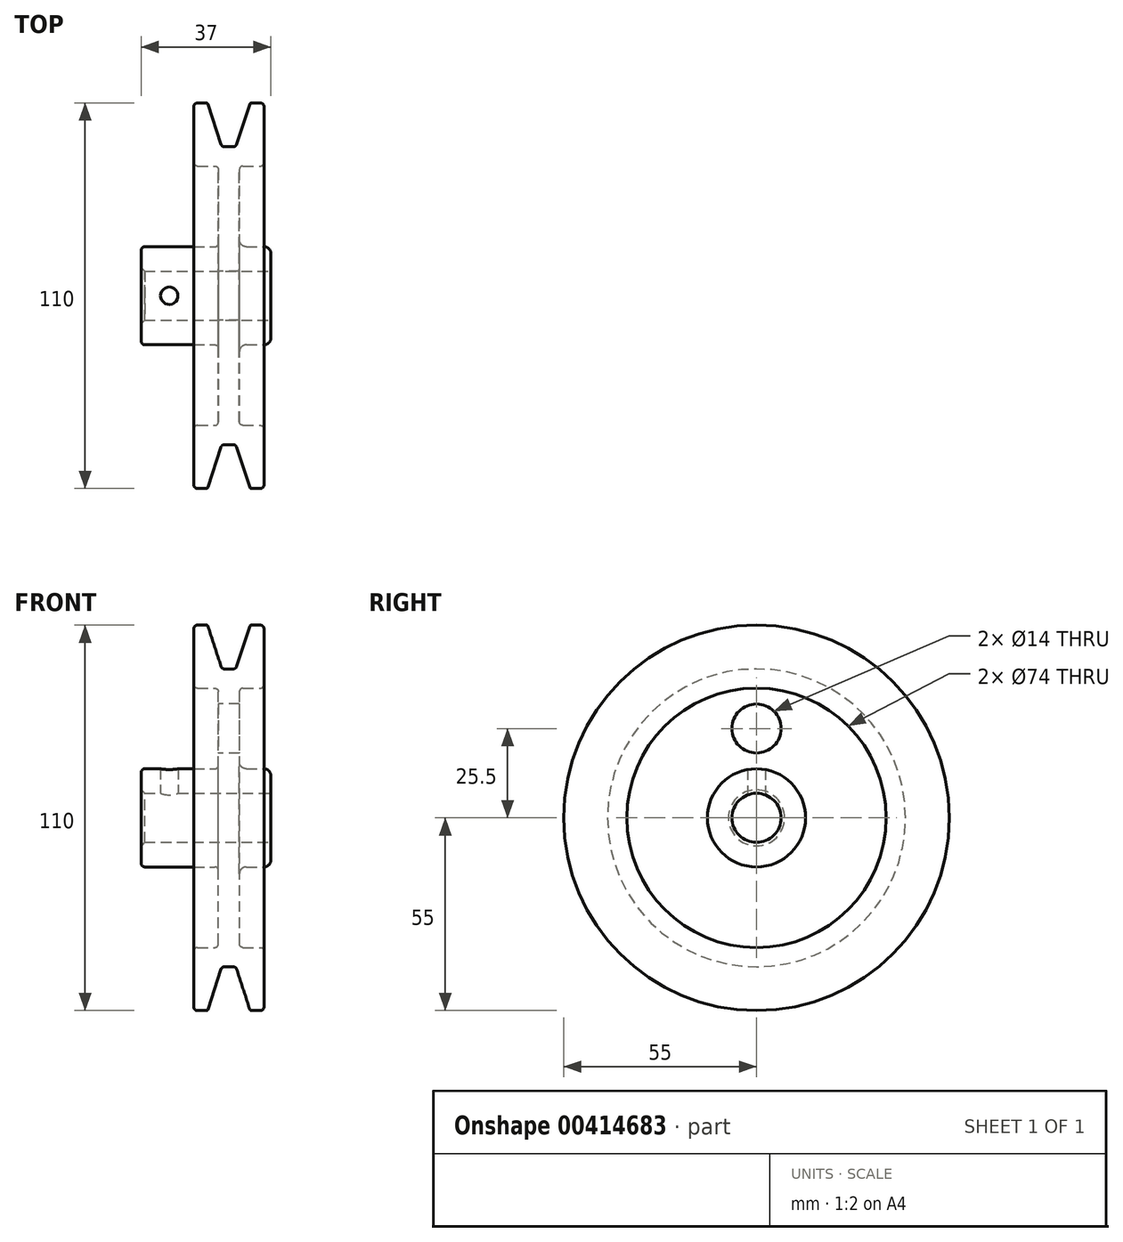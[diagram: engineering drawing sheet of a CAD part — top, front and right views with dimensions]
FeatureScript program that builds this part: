
annotation { "Feature Type Name" : "Feature", "Feature Type Description" : "" }
export const myFeature = defineFeature(function(context is Context, id is Id, definition is map)
    precondition{}
    {
        {
            var Q0;
            Q0=qCreatedBy(makeId("Front.planeOp"),FACE);
            var sketch = newSketch(context, id + "F0", { "sketchPlane" : qUnion([Q0])});
            skLineSegment(sketch, "E0", {"start": v(0, 0) * mm, "end": v(-34.66, 0) * mm, "construction": true});
            skLineSegment(sketch, "E1", {"start": v(0, 7) * mm, "end": v(-37, 7) * mm});
            skLineSegment(sketch, "E2", {"start": v(-37, 7) * mm, "end": v(-37, 14) * mm});
            skLineSegment(sketch, "E3", {"start": v(-37, 14) * mm, "end": v(-15, 14) * mm});
            skLineSegment(sketch, "E4", {"start": v(-15, 14) * mm, "end": v(-15, 37) * mm});
            skLineSegment(sketch, "E5", {"start": v(-15, 37) * mm, "end": v(-22, 37) * mm});
            skLineSegment(sketch, "E6", {"start": v(-22, 37) * mm, "end": v(-22, 55) * mm});
            skLineSegment(sketch, "E7", {"start": v(-22, 55) * mm, "end": v(-18.43, 55) * mm});
            skLineSegment(sketch, "E8", {"start": v(-17.95, 54.65) * mm, "end": v(-14, 42.5) * mm});
            skLineSegment(sketch, "E9", {"start": v(-14, 42.5) * mm, "end": v(-10, 42.5) * mm});
            skLineSegment(sketch, "E10", {"start": v(-10, 42.5) * mm, "end": v(-6.05, 54.65) * mm});
            skLineSegment(sketch, "E11", {"start": v(-5.57, 55) * mm, "end": v(-2, 55) * mm});
            skLineSegment(sketch, "E12", {"start": v(-2, 55) * mm, "end": v(-2, 37) * mm});
            skLineSegment(sketch, "E13", {"start": v(-2, 37) * mm, "end": v(-9, 37) * mm});
            skLineSegment(sketch, "E14", {"start": v(-9, 37) * mm, "end": v(-9, 16) * mm});
            skLineSegment(sketch, "E15", {"start": v(-7, 14) * mm, "end": v(-2, 14) * mm});
            skLineSegment(sketch, "E16", {"start": v(0, 12) * mm, "end": v(0, 7) * mm});
            skLineSegment(sketch, "E17", {"start": v(-26.57, 50.5) * mm, "end": v(1.51, 50.5) * mm, "construction": true});
            skLineSegment(sketch, "E18", {"start": v(-12, 42.5) * mm, "end": v(-12, 57.22) * mm, "construction": true});
            skPoint(sketch, "E19", {"position": v(-16.6, 50.5) * mm});
            skPoint(sketch, "E20", {"position": v(-7.4, 50.5) * mm});
            skPoint(sketch, "E21.visualSharp", {"position": v(-18.06, 55) * mm});
            skArc(sketch, "E21.filletArc", {"start": v(-17.95, 54.65) * mm, "mid": v(-18.13, 54.9) * mm, "end": v(-18.43, 55) * mm});
            skPoint(sketch, "E22.visualSharp", {"position": v(-5.94, 55) * mm});
            skArc(sketch, "E22.filletArc", {"start": v(-5.57, 55) * mm, "mid": v(-5.87, 54.9) * mm, "end": v(-6.05, 54.65) * mm});
            skPoint(sketch, "E23.visualSharp", {"position": v(-9, 14) * mm});
            skArc(sketch, "E23.filletArc", {"start": v(-9, 16) * mm, "mid": v(-8.41, 14.59) * mm, "end": v(-7, 14) * mm});
            skPoint(sketch, "E24.visualSharp", {"position": v(0, 14) * mm});
            skArc(sketch, "E24.filletArc", {"start": v(0, 12) * mm, "mid": v(-0.59, 13.41) * mm, "end": v(-2, 14) * mm});
            skSolve(sketch);
        }
        {
            var Q0;
            Q0 = qSketchRegion(id + "F0", true);
            var Q1;
            Q1=sQuery(id+"F0.wireOp",EDGE,"E0");
            revolve(context, id + "F1", {"entities" : qUnion([Q0]), "axis" : qUnion([Q1]), "revolveType" : RevolveType.FULL});
        }
        {
            var Q0;
            Q0=makeQuery(id+"F1.opRevolve","SWEPT_FACE",FACE,{"disambiguationData":[OSD([sQuery(id+"F0.wireOp",EDGE,"E4")])]});
            var sketch = newSketch(context, id + "F2", { "sketchPlane" : qUnion([Q0])});
            skCircle(sketch, "E25", {"center": v(0, 0) * mm, "radius": 25.5 * mm, "construction": true});
            skCircle(sketch, "E26", {"center": v(0, 25.5) * mm, "radius": 7 * mm});
            skSolve(sketch);
        }
        {
            var Q0;
            Q0=makeQuery(id+"F2.imprint","IMPRINT",FACE,{"disambiguationData":[TD([[makeQuery(id+"F2.imprint","IMPRINT",EDGE,{"derivedFrom":sQuery(id+"F2.wireOp",EDGE,"E26")}),1.0]])]});
            extrude(context, id + "F3", {"entities" : qUnion([Q0]), "operationType" : NewBodyOperationType.REMOVE, "endBound" : BoundingType.UP_TO_NEXT, "oppositeDirection" : true, "depth" : 25 * mm});
        }
        {
            var Q0;
            Q0=qCreatedBy(makeId("Top.planeOp"),FACE);
            var sketch = newSketch(context, id + "F4", { "sketchPlane" : qUnion([Q0])});
            skCircle(sketch, "E27", {"center": v(-29, 0) * mm, "radius": 2.5 * mm});
            skSolve(sketch);
        }
        {
            var Q0;
            Q0 = qSketchRegion(id + "F4", true);
            var Q1;
            Q1=makeQuery(id+"F1.opRevolve","SWEPT_FACE",FACE,{"disambiguationData":[OSD([sQuery(id+"F0.wireOp",EDGE,"E6")])]});
            var Q2;
            Q2=makeQuery(id+"F1.opRevolve","SWEPT_BODY",BODY,{"disambiguationData":[OSD([sQuery(id+"F0.wireOp",EDGE,"E1"),sQuery(id+"F0.wireOp",EDGE,"E2"),sQuery(id+"F0.wireOp",EDGE,"E3"),sQuery(id+"F0.wireOp",EDGE,"E4"),sQuery(id+"F0.wireOp",EDGE,"E5"),sQuery(id+"F0.wireOp",EDGE,"E6"),sQuery(id+"F0.wireOp",EDGE,"E7"),sQuery(id+"F0.wireOp",EDGE,"E8"),sQuery(id+"F0.wireOp",EDGE,"E9"),sQuery(id+"F0.wireOp",EDGE,"E10"),sQuery(id+"F0.wireOp",EDGE,"E11"),sQuery(id+"F0.wireOp",EDGE,"E12"),sQuery(id+"F0.wireOp",EDGE,"E13"),sQuery(id+"F0.wireOp",EDGE,"E14"),sQuery(id+"F0.wireOp",EDGE,"E15"),sQuery(id+"F0.wireOp",EDGE,"E16"),sQuery(id+"F0.wireOp",EDGE,"E21.filletArc"),sQuery(id+"F0.wireOp",EDGE,"E22.filletArc"),sQuery(id+"F0.wireOp",EDGE,"E23.filletArc"),sQuery(id+"F0.wireOp",EDGE,"E24.filletArc")])]});
            extrude(context, id + "F5", {"entities" : qUnion([Q0]), "operationType" : NewBodyOperationType.REMOVE, "endBound" : BoundingType.THROUGH_ALL, "endBoundEntityFace" : qUnion([Q1]), "endBoundEntityBody" : qUnion([Q2]), "depth" : 25 * mm});
        }
        {
            var Q0;
            Q0=makeQuery(id+"F1.opRevolve","SWEPT_EDGE",EDGE,{"disambiguationData":[OSD([sQuery(id+"F0.wireOp",EDGE,"E1"),sQuery(id+"F0.wireOp",EDGE,"E2")])]});
            chamfer(context, id + "F6", {"entities" : qUnion([Q0]), "width" : 1 * mm, "tangentPropagation" : true});
        }
        {
            var Q0;
            Q0=makeQuery(id+"F1.opRevolve","SWEPT_EDGE",EDGE,{"disambiguationData":[OSD([sQuery(id+"F0.wireOp",EDGE,"E2"),sQuery(id+"F0.wireOp",EDGE,"E3")])]});
            var Q1;
            Q1=makeQuery(id+"F1.opRevolve","SWEPT_EDGE",EDGE,{"disambiguationData":[OSD([sQuery(id+"F0.wireOp",EDGE,"E4"),sQuery(id+"F0.wireOp",EDGE,"E5")])]});
            var Q2;
            Q2=makeQuery(id+"F1.opRevolve","SWEPT_EDGE",EDGE,{"disambiguationData":[OSD([sQuery(id+"F0.wireOp",EDGE,"E5"),sQuery(id+"F0.wireOp",EDGE,"E6")])]});
            var Q3;
            Q3=makeQuery(id+"F1.opRevolve","SWEPT_EDGE",EDGE,{"disambiguationData":[OSD([sQuery(id+"F0.wireOp",EDGE,"E6"),sQuery(id+"F0.wireOp",EDGE,"E7")])]});
            var Q4;
            Q4=makeQuery(id+"F1.opRevolve","SWEPT_EDGE",EDGE,{"disambiguationData":[OSD([sQuery(id+"F0.wireOp",EDGE,"E3"),sQuery(id+"F0.wireOp",EDGE,"E4")])]});
            var Q5;
            Q5=makeQuery(id+"F3.boolean.opBoolean","COPY",EDGE,{"derivedFrom":makeQuery(id+"F3.opExtrude","CAP_EDGE",EDGE,{"disambiguationData":[OSD([sQuery(id+"F2.wireOp",EDGE,"E26")])],"isStart":true})});
            var Q6;
            Q6=makeQuery(id+"FefsIZx4eyhpBWJ_1.3.F3.boolean.opBoolean","COPY",EDGE,{"derivedFrom":makeQuery(id+"FefsIZx4eyhpBWJ_1.3.F3.opExtrude","CAP_EDGE",EDGE,{"disambiguationData":[OSD([sQuery(id+"F2.wireOp",EDGE,"E26")])],"isStart":true})});
            var Q7;
            Q7=makeQuery(id+"FefsIZx4eyhpBWJ_1.2.F3.boolean.opBoolean","COPY",EDGE,{"derivedFrom":makeQuery(id+"FefsIZx4eyhpBWJ_1.2.F3.opExtrude","CAP_EDGE",EDGE,{"disambiguationData":[OSD([sQuery(id+"F2.wireOp",EDGE,"E26")])],"isStart":true})});
            var Q8;
            Q8=makeQuery(id+"FefsIZx4eyhpBWJ_1.1.F3.boolean.opBoolean","COPY",EDGE,{"derivedFrom":makeQuery(id+"FefsIZx4eyhpBWJ_1.1.F3.opExtrude","CAP_EDGE",EDGE,{"disambiguationData":[OSD([sQuery(id+"F2.wireOp",EDGE,"E26")])],"isStart":true})});
            var Q9;
            Q9=makeQuery(id+"F1.opRevolve","SWEPT_EDGE",EDGE,{"disambiguationData":[OSD([sQuery(id+"F0.wireOp",EDGE,"E11"),sQuery(id+"F0.wireOp",EDGE,"E12")])]});
            var Q10;
            Q10=makeQuery(id+"F1.opRevolve","SWEPT_EDGE",EDGE,{"disambiguationData":[OSD([sQuery(id+"F0.wireOp",EDGE,"E12"),sQuery(id+"F0.wireOp",EDGE,"E13")])]});
            var Q11;
            Q11=makeQuery(id+"F1.opRevolve","SWEPT_EDGE",EDGE,{"disambiguationData":[OSD([sQuery(id+"F0.wireOp",EDGE,"E13"),sQuery(id+"F0.wireOp",EDGE,"E14")])]});
            var Q12;
            Q12=makeQuery(id+"F3.boolean.opBoolean","COPY",EDGE,{"derivedFrom":makeQuery(id+"F3.opExtrude","CAP_EDGE",EDGE,{"disambiguationData":[OSD([sQuery(id+"F2.wireOp",EDGE,"E26")])],"isStart":false})});
            var Q13;
            Q13=makeQuery(id+"FefsIZx4eyhpBWJ_1.3.F3.boolean.opBoolean","COPY",EDGE,{"derivedFrom":makeQuery(id+"FefsIZx4eyhpBWJ_1.3.F3.opExtrude","CAP_EDGE",EDGE,{"disambiguationData":[OSD([sQuery(id+"F2.wireOp",EDGE,"E26")])],"isStart":false})});
            var Q14;
            Q14=makeQuery(id+"FefsIZx4eyhpBWJ_1.2.F3.boolean.opBoolean","COPY",EDGE,{"derivedFrom":makeQuery(id+"FefsIZx4eyhpBWJ_1.2.F3.opExtrude","CAP_EDGE",EDGE,{"disambiguationData":[OSD([sQuery(id+"F2.wireOp",EDGE,"E26")])],"isStart":false})});
            var Q15;
            Q15=makeQuery(id+"FefsIZx4eyhpBWJ_1.1.F3.boolean.opBoolean","COPY",EDGE,{"derivedFrom":makeQuery(id+"FefsIZx4eyhpBWJ_1.1.F3.opExtrude","CAP_EDGE",EDGE,{"disambiguationData":[OSD([sQuery(id+"F2.wireOp",EDGE,"E26")])],"isStart":false})});
            var Q16;
            Q16=makeQuery(id+"F1.opRevolve","SWEPT_EDGE",EDGE,{"disambiguationData":[OSD([sQuery(id+"F0.wireOp",EDGE,"E8"),sQuery(id+"F0.wireOp",EDGE,"E9")])]});
            var Q17;
            Q17=makeQuery(id+"F1.opRevolve","SWEPT_EDGE",EDGE,{"disambiguationData":[OSD([sQuery(id+"F0.wireOp",EDGE,"E9"),sQuery(id+"F0.wireOp",EDGE,"E10")])]});
            fillet(context, id + "F7", {"entities" : qUnion([Q0, Q1, Q2, Q3, Q4, Q5, Q6, Q7, Q8, Q9, Q10, Q11, Q12, Q13, Q14, Q15, Q16, Q17]), "radius" : 1 * mm, "tangentPropagation" : true, "allowEdgeOverflow" : false});
        }
    });
